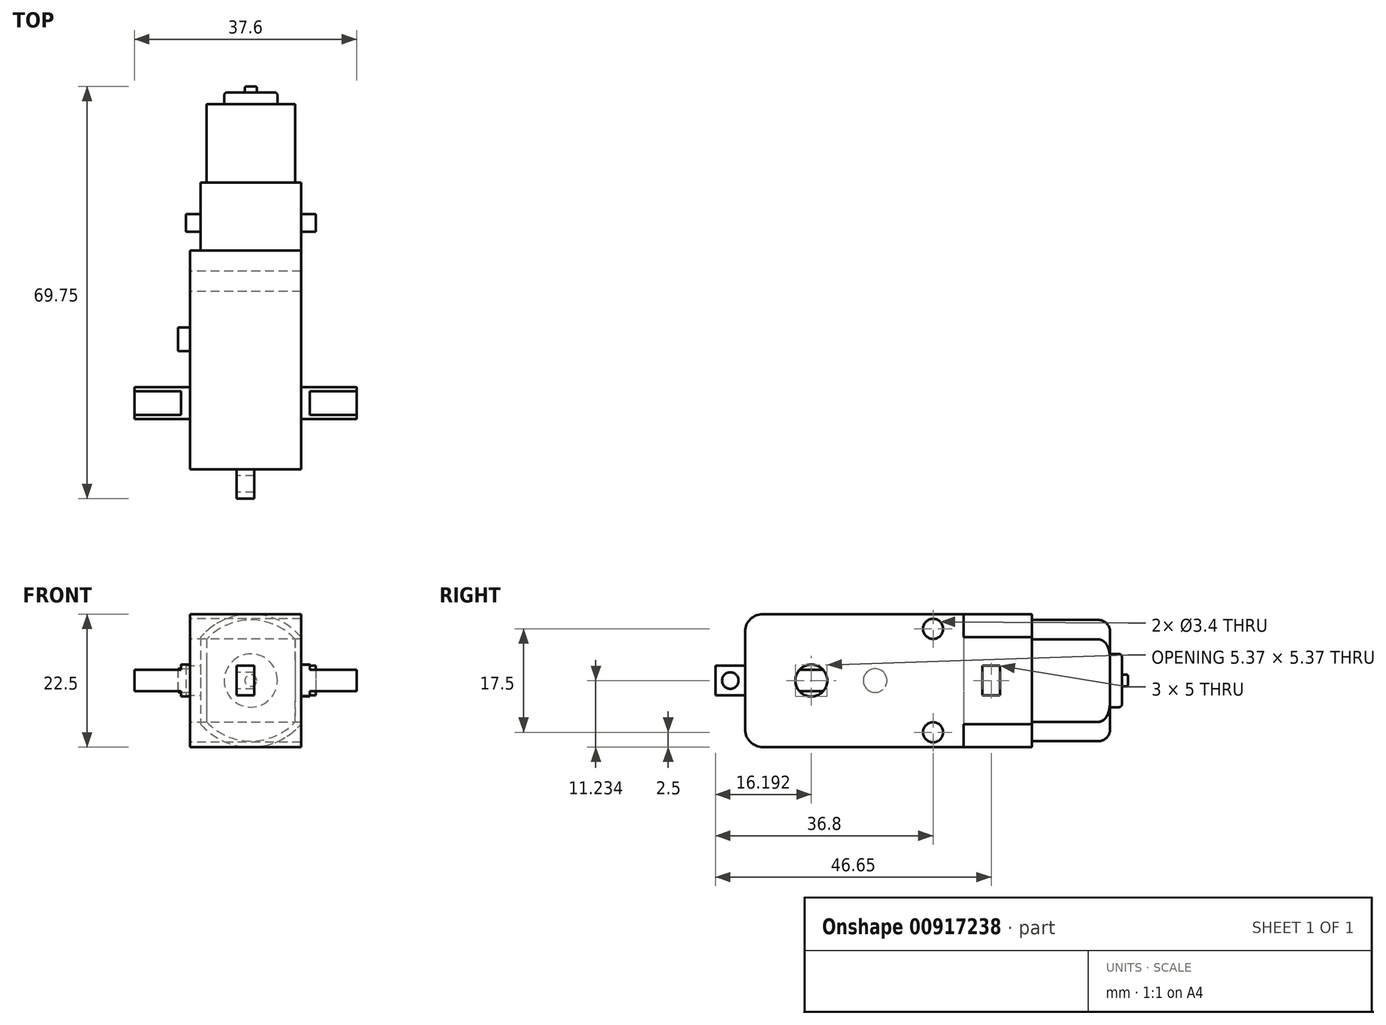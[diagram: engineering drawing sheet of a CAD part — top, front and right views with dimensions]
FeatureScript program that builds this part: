
annotation { "Feature Type Name" : "Feature", "Feature Type Description" : "" }
export const myFeature = defineFeature(function(context is Context, id is Id, definition is map)
    precondition{}
    {
        {
            var Q0;
            Q0=qCreatedBy(makeId("Right.planeOp"),FACE);
            var sketch = newSketch(context, id + "F0", { "sketchPlane" : qUnion([Q0])});
            skLineSegment(sketch, "E0.bottom", {"start": v(0, 11.25) * mm, "end": v(-34, 11.25) * mm});
            skLineSegment(sketch, "E0.top", {"start": v(0, -11.25) * mm, "end": v(-34, -11.25) * mm});
            skLineSegment(sketch, "E0.left", {"start": v(0, 11.25) * mm, "end": v(0, -11.25) * mm});
            skLineSegment(sketch, "E0.right", {"start": v(-37, 8.25) * mm, "end": v(-37, -8.25) * mm});
            skCircle(sketch, "E1", {"center": v(-25.8, 0) * mm, "radius": 2.7 * mm});
            skCircle(sketch, "E2", {"center": v(-5.2, 8.75) * mm, "radius": 1.7 * mm});
            skCircle(sketch, "E3.MirrorC", {"center": v(-5.2, -8.75) * mm, "radius": 1.7 * mm});
            skLineSegment(sketch, "E4.bottom", {"start": v(-37, 2.5) * mm, "end": v(-42, 2.5) * mm});
            skLineSegment(sketch, "E4.top", {"start": v(-37, -2.5) * mm, "end": v(-42, -2.5) * mm});
            skLineSegment(sketch, "E4.left", {"start": v(-37, 2.5) * mm, "end": v(-37, -2.5) * mm});
            skLineSegment(sketch, "E4.right", {"start": v(-42, 2.5) * mm, "end": v(-42, -2.5) * mm});
            skCircle(sketch, "E5", {"center": v(-39.5, 0) * mm, "radius": 1.4 * mm});
            skPoint(sketch, "E6", {"position": v(-39.5, 2.5) * mm});
            skLineSegment(sketch, "E7", {"start": v(-23.79, 1.8) * mm, "end": v(-27.81, 1.8) * mm});
            skLineSegment(sketch, "E8", {"start": v(-23.79, -1.8) * mm, "end": v(-27.81, -1.8) * mm});
            skPoint(sketch, "E9.visualSharp", {"position": v(-37, 11.25) * mm});
            skArc(sketch, "E9.filletArc", {"start": v(-34, 11.25) * mm, "mid": v(-36.12, 10.37) * mm, "end": v(-37, 8.25) * mm});
            skPoint(sketch, "E10.visualSharp", {"position": v(-37, -11.25) * mm});
            skArc(sketch, "E10.filletArc", {"start": v(-37, -8.25) * mm, "mid": v(-36.12, -10.37) * mm, "end": v(-34, -11.25) * mm});
            skSolve(sketch);
        }
        {
            var Q0;
            {var subQ1=sQuery(id+"F0.wireOp",EDGE,"E0.bottom");Q0=makeQuery(id+"F0.imprint","IMPRINT",FACE,{"disambiguationData":[TD([[makeQuery(id+"F0.imprint","IMPRINT",EDGE,{"derivedFrom":subQ1}),1.0]])]});}
            extrude(context, id + "F1", {"entities" : qUnion([Q0]), "depth" : 18.8 * mm, "offsetDistance" : 25 * mm, "symmetric" : true});
        }
        {
            var Q0;
            Q0=makeQuery(id+"F0.imprint","IMPRINT",FACE,{"disambiguationData":[TD([[makeQuery(id+"F0.imprint","IMPRINT",EDGE,{"derivedFrom":sQuery(id+"F0.wireOp",EDGE,"E4.bottom")}),1.0]])]});
            extrude(context, id + "F2", {"entities" : qUnion([Q0]), "operationType" : NewBodyOperationType.ADD, "depth" : 3 * mm, "offsetDistance" : 25 * mm, "symmetric" : true});
        }
        {
            var Q0;
            {var subQ0=sQuery(id+"F0.wireOp",EDGE,"E7");Q0=makeQuery(id+"F0.imprint","IMPRINT",FACE,{"disambiguationData":[TD([[makeQuery(id+"F0.imprint","IMPRINT",EDGE,{"derivedFrom":subQ0}),-1.0]])]});}
            var Q1;
            {var subQ0=sQuery(id+"F0.wireOp",EDGE,"E8");Q1=makeQuery(id+"F0.imprint","IMPRINT",FACE,{"disambiguationData":[TD([[makeQuery(id+"F0.imprint","IMPRINT",EDGE,{"derivedFrom":subQ0}),1.0]])]});}
            var Q2;
            {var subQ0=sQuery(id+"F0.wireOp",EDGE,"E7");Q2=makeQuery(id+"F0.imprint","IMPRINT",FACE,{"disambiguationData":[TD([[makeQuery(id+"F0.imprint","IMPRINT",EDGE,{"derivedFrom":subQ0}),1.0]])]});}
            extrude(context, id + "F3", {"entities" : qUnion([Q0, Q1, Q2]), "depth" : 21.8 * mm, "offsetDistance" : 25 * mm, "symmetric" : true});
        }
        {
            var Q0;
            Q0=makeQuery(id+"F0.imprint","IMPRINT",FACE,{"disambiguationData":[TD([[makeQuery(id+"F0.imprint","IMPRINT",EDGE,{"derivedFrom":sQuery(id+"F0.wireOp",EDGE,"E1")}),1.0]])]});
            extrude(context, id + "F4", {"entities" : qUnion([Q0]), "operationType" : NewBodyOperationType.ADD, "depth" : 37.6 * mm, "offsetDistance" : 25 * mm, "symmetric" : true});
        }
        {
            var Q0;
            Q0=makeQuery(id+"F1.opExtrude","CAP_FACE",FACE,{"disambiguationData":[OSD([sQuery(id+"F0.wireOp",EDGE,"E0.bottom"),sQuery(id+"F0.wireOp",EDGE,"E0.top"),sQuery(id+"F0.wireOp",EDGE,"E0.left"),sQuery(id+"F0.wireOp",EDGE,"E0.right"),sQuery(id+"F0.wireOp",EDGE,"E1"),sQuery(id+"F0.wireOp",EDGE,"E2"),sQuery(id+"F0.wireOp",EDGE,"E3.MirrorC"),sQuery(id+"F0.wireOp",EDGE,"E4.left"),sQuery(id+"F0.wireOp",EDGE,"E9.filletArc"),sQuery(id+"F0.wireOp",EDGE,"E10.filletArc")])],"isStart":true});
            var sketch = newSketch(context, id + "F5", { "sketchPlane" : qUnion([Q0])});
            skCircle(sketch, "E11", {"center": v(15, 0) * mm, "radius": 2 * mm});
            skSolve(sketch);
        }
        {
            var Q0;
            Q0=makeQuery(id+"F5.imprint","IMPRINT",FACE,{"disambiguationData":[TD([[makeQuery(id+"F5.imprint","IMPRINT",EDGE,{"derivedFrom":sQuery(id+"F5.wireOp",EDGE,"E11")}),1.0]])]});
            extrude(context, id + "F6", {"entities" : qUnion([Q0]), "operationType" : NewBodyOperationType.ADD, "depth" : 2 * mm, "offsetDistance" : 25 * mm});
        }
        {
            var Q0;
            Q0=makeQuery(id+"F1.opExtrude","SWEPT_FACE",FACE,{"disambiguationData":[OSD([sQuery(id+"F0.wireOp",EDGE,"E0.left")])]});
            var sketch = newSketch(context, id + "F7", { "sketchPlane" : qUnion([Q0])});
            skLineSegment(sketch, "E12.bottom", {"start": v(-9.4, 11.25) * mm, "end": v(7.6, 11.25) * mm});
            skLineSegment(sketch, "E12.top", {"start": v(-9.4, -11.25) * mm, "end": v(7.6, -11.25) * mm});
            skLineSegment(sketch, "E12.left", {"start": v(-9.4, 11.25) * mm, "end": v(-9.4, -11.25) * mm});
            skLineSegment(sketch, "E12.right", {"start": v(7.6, 11.25) * mm, "end": v(7.6, -11.25) * mm});
            skPoint(sketch, "E13.visualSharp", {"position": v(-9.4, 11.25) * mm});
            skCircle(sketch, "E14", {"center": v(-0.9, 0) * mm, "radius": 11.25 * mm});
            skPoint(sketch, "E15", {"position": v(-0.9, 11.25) * mm});
            skPoint(sketch, "E16", {"position": v(-9.4, 7.37) * mm});
            skPoint(sketch, "E17", {"position": v(-9.4, -7.37) * mm});
            skPoint(sketch, "E18", {"position": v(7.6, -7.37) * mm});
            skPoint(sketch, "E19", {"position": v(7.6, 7.37) * mm});
            skSolve(sketch);
        }
        {
            var Q0;
            {var subQ0=sQuery(id+"F7.wireOp",EDGE,"E14");var subQ2=sQuery(id+"F7.wireOp",EDGE,"E12.left");var subQ3=makeQuery(id+"F7.imprint","INTERSECT",VERTEX,{"disambiguationData":[OD(0.0)],"derivedFrom":[subQ2,subQ0]});Q0=makeQuery(id+"F7.imprint","IMPRINT",FACE,{"disambiguationData":[TD([[makeQuery(id+"F7.imprint","IMPRINT",EDGE,{"disambiguationData":[TD([[subQ3,-1.0]])],"derivedFrom":subQ2}),1.0]])]});}
            extrude(context, id + "F8", {"entities" : qUnion([Q0]), "operationType" : NewBodyOperationType.ADD, "depth" : 11.5 * mm, "offsetDistance" : 25 * mm});
        }
        {
            var Q0;
            Q0=makeQuery(id+"F8.opExtrude","CAP_FACE",FACE,{"disambiguationData":[OSD([sQuery(id+"F7.wireOp",EDGE,"E12.left"),sQuery(id+"F7.wireOp",EDGE,"E12.right"),sQuery(id+"F7.wireOp",EDGE,"E14")])],"isStart":false});
            var sketch = newSketch(context, id + "F9", { "sketchPlane" : qUnion([Q0])});
            skArc(sketch, "E20.0", {"start": v(6.6, 6.99) * mm, "mid": v(-0.9, 10.25) * mm, "end": v(-8.4, 6.99) * mm});
            skLineSegment(sketch, "E20.1", {"start": v(6.6, 6.99) * mm, "end": v(6.6, -6.99) * mm});
            skArc(sketch, "E20.2", {"start": v(-8.4, -6.99) * mm, "mid": v(-0.9, -10.25) * mm, "end": v(6.6, -6.99) * mm});
            skLineSegment(sketch, "E20.3", {"start": v(-8.4, 6.99) * mm, "end": v(-8.4, -6.99) * mm});
            skSolve(sketch);
        }
        {
            var Q0;
            Q0=makeQuery(id+"F9.imprint","IMPRINT",FACE,{"disambiguationData":[TD([[makeQuery(id+"F9.imprint","IMPRINT",EDGE,{"derivedFrom":sQuery(id+"F9.wireOp",EDGE,"E20.0")}),1.0]])]});
            extrude(context, id + "F10", {"entities" : qUnion([Q0]), "depth" : 13.25 * mm, "offsetDistance" : 25 * mm});
        }
        {
            var Q0;
            Q0=makeQuery(id+"F10.opExtrude","CAP_EDGE",EDGE,{"disambiguationData":[OSD([sQuery(id+"F9.wireOp",EDGE,"E20.0")])],"isStart":false});
            var Q1;
            Q1=makeQuery(id+"F10.opExtrude","CAP_EDGE",EDGE,{"disambiguationData":[OSD([sQuery(id+"F9.wireOp",EDGE,"E20.2")])],"isStart":false});
            fillet(context, id + "F11", {"entities" : qUnion([Q0, Q1]), "radius" : 2 * mm, "tangentPropagation" : true, "allowEdgeOverflow" : false});
        }
        {
            var Q0;
            Q0=makeQuery(id+"F10.opExtrude","CAP_FACE",FACE,{"disambiguationData":[OSD([sQuery(id+"F9.wireOp",EDGE,"E20.0"),sQuery(id+"F9.wireOp",EDGE,"E20.1"),sQuery(id+"F9.wireOp",EDGE,"E20.2"),sQuery(id+"F9.wireOp",EDGE,"E20.3")])],"isStart":false});
            var sketch = newSketch(context, id + "F12", { "sketchPlane" : qUnion([Q0])});
            skCircle(sketch, "E21", {"center": v(-0.9, 0) * mm, "radius": 4.5 * mm});
            skCircle(sketch, "E22", {"center": v(-0.9, 0) * mm, "radius": 1 * mm});
            skSolve(sketch);
        }
        {
            var Q0;
            Q0=makeQuery(id+"F12.imprint","IMPRINT",FACE,{"disambiguationData":[TD([[makeQuery(id+"F12.imprint","IMPRINT",EDGE,{"derivedFrom":sQuery(id+"F12.wireOp",EDGE,"E21")}),1.0]])]});
            extrude(context, id + "F13", {"entities" : qUnion([Q0]), "operationType" : NewBodyOperationType.ADD, "depth" : 2 * mm, "offsetDistance" : 25 * mm});
        }
        {
            var Q0;
            Q0=makeQuery(id+"F13.opExtrude","CAP_EDGE",EDGE,{"disambiguationData":[OSD([sQuery(id+"F12.wireOp",EDGE,"E21")])],"isStart":false});
            fillet(context, id + "F14", {"entities" : qUnion([Q0]), "radius" : 0.5 * mm, "tangentPropagation" : true, "allowEdgeOverflow" : false});
        }
        {
            var Q0;
            Q0=makeQuery(id+"F13.boolean.opBoolean","SPLIT",FACE,{"disambiguationData":[TD([makeQuery(id+"F13.opExtrude","SWEPT_FACE",FACE,{"disambiguationData":[OSD([sQuery(id+"F12.wireOp",EDGE,"E22")])]})])],"derivedFrom":makeQuery(id+"F10.opExtrude","CAP_FACE",FACE,{"disambiguationData":[OSD([sQuery(id+"F9.wireOp",EDGE,"E20.0"),sQuery(id+"F9.wireOp",EDGE,"E20.1"),sQuery(id+"F9.wireOp",EDGE,"E20.2"),sQuery(id+"F9.wireOp",EDGE,"E20.3")])],"isStart":false})});
            extrude(context, id + "F15", {"entities" : qUnion([Q0]), "operationType" : NewBodyOperationType.ADD, "depth" : 3 * mm, "offsetDistance" : 25 * mm});
        }
        {
            var Q0;
            Q0=makeQuery(id+"F15.opExtrude","CAP_EDGE",EDGE,{"disambiguationData":[OSD([sQuery(id+"F12.wireOp",EDGE,"E22")])],"isStart":false});
            fillet(context, id + "F16", {"entities" : qUnion([Q0]), "radius" : 0.2 * mm, "tangentPropagation" : true, "defaultsChanged" : false, "vertexSettings" : [], "allowEdgeOverflow" : false});
        }
        {
            var Q0;
            Q0=qCreatedBy(makeId("Top.planeOp"),FACE);
            var sketch = newSketch(context, id + "F17", { "sketchPlane" : qUnion([Q0])});
            skLineSegment(sketch, "E23.bottom", {"start": v(11.9, 3.15) * mm, "end": v(9.4, 3.15) * mm});
            skLineSegment(sketch, "E23.top", {"start": v(11.9, 6.15) * mm, "end": v(9.4, 6.15) * mm});
            skLineSegment(sketch, "E23.left", {"start": v(11.9, 3.15) * mm, "end": v(11.9, 6.15) * mm});
            skLineSegment(sketch, "E23.right", {"start": v(9.4, 3.15) * mm, "end": v(9.4, 6.15) * mm});
            skLineSegment(sketch, "E24", {"start": v(0.9, 1.54) * mm, "end": v(0.9, 14.47) * mm, "construction": true});
            skLineSegment(sketch, "E25.MirrorCS", {"start": v(-10.1, 6.15) * mm, "end": v(-7.6, 6.15) * mm});
            skLineSegment(sketch, "E26.MirrorCS", {"start": v(-10.1, 3.15) * mm, "end": v(-10.1, 6.15) * mm});
            skLineSegment(sketch, "E27.MirrorCS", {"start": v(-10.1, 3.15) * mm, "end": v(-7.6, 3.15) * mm});
            skLineSegment(sketch, "E28.MirrorCS", {"start": v(-7.6, 3.15) * mm, "end": v(-7.6, 6.15) * mm});
            skSolve(sketch);
        }
        {
            var Q0;
            Q0 = qSketchRegion(id + "F17", true);
            extrude(context, id + "F18", {"entities" : qUnion([Q0]), "operationType" : NewBodyOperationType.ADD, "depth" : 5 * mm, "offsetDistance" : 25 * mm, "symmetric" : true});
        }
    });
